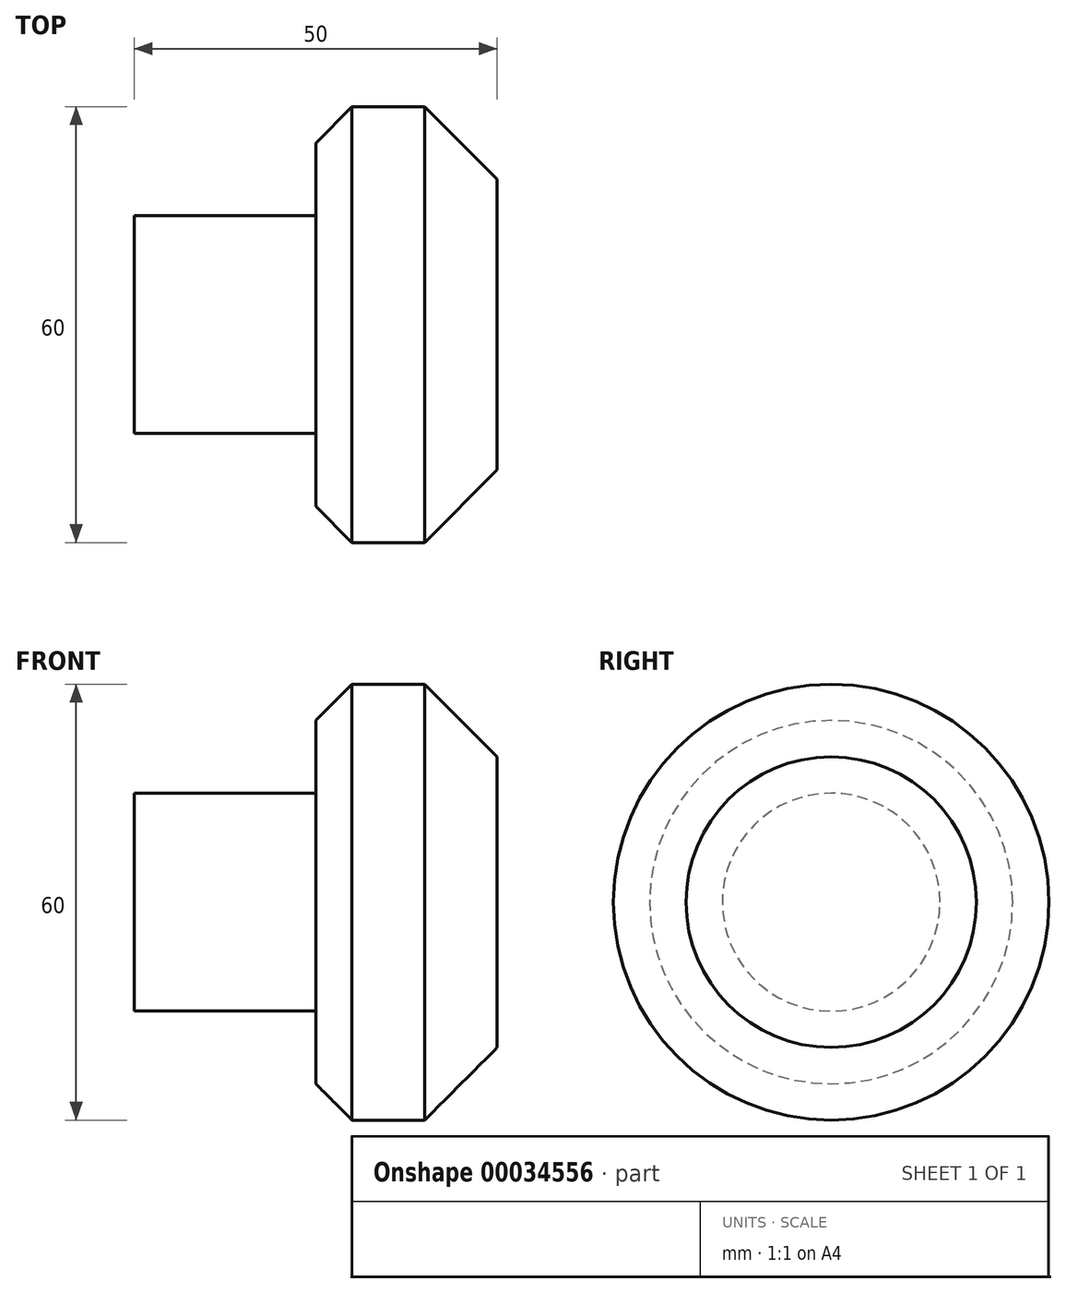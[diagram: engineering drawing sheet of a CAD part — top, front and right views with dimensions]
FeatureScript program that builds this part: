
annotation { "Feature Type Name" : "Feature", "Feature Type Description" : "" }
export const myFeature = defineFeature(function(context is Context, id is Id, definition is map)
    precondition{}
    {
        {
            var Q0;
            Q0=qCreatedBy(makeId("Right.planeOp"),FACE);
            var sketch = newSketch(context, id + "F0", { "sketchPlane" : qUnion([Q0])});
            skCircle(sketch, "E0", {"center": v(0, 0) * mm, "radius": 15 * mm});
            skSolve(sketch);
        }
        {
            var Q0;
            Q0 = qSketchRegion(id + "F0", true);
            extrude(context, id + "F4", {"entities" : qUnion([Q0]), "depth" : 25 * mm});
        }
        {
            var Q0;
            Q0=makeQuery(id+"F4.opExtrude","CAP_FACE",FACE,{"disambiguationData":[OSD([sQuery(id+"F0.wireOp",EDGE,"E0")])],"isStart":false});
            var sketch = newSketch(context, id + "F1", { "sketchPlane" : qUnion([Q0])});
            skCircle(sketch, "E1", {"center": v(0, 0) * mm, "radius": 30 * mm});
            skSolve(sketch);
        }
        {
            var Q0;
            Q0 = qSketchRegion(id + "F1", true);
            extrude(context, id + "F5", {"entities" : qUnion([Q0]), "operationType" : NewBodyOperationType.ADD, "depth" : 25 * mm});
        }
        {
            var Q0;
            Q0=makeQuery(id+"F5.opExtrude","CAP_EDGE",EDGE,{"disambiguationData":[OSD([sQuery(id+"F1.wireOp",EDGE,"E1")])],"isStart":false});
            chamfer(context, id + "F2", {"entities" : qUnion([Q0]), "width" : 10 * mm, "tangentPropagation" : true});
        }
        {
            var Q0;
            Q0=makeQuery(id+"F5.opExtrude","CAP_EDGE",EDGE,{"disambiguationData":[OSD([sQuery(id+"F1.wireOp",EDGE,"E1")])],"isStart":true});
            chamfer(context, id + "F3", {"entities" : qUnion([Q0]), "width" : 5 * mm, "tangentPropagation" : true});
        }
    });
